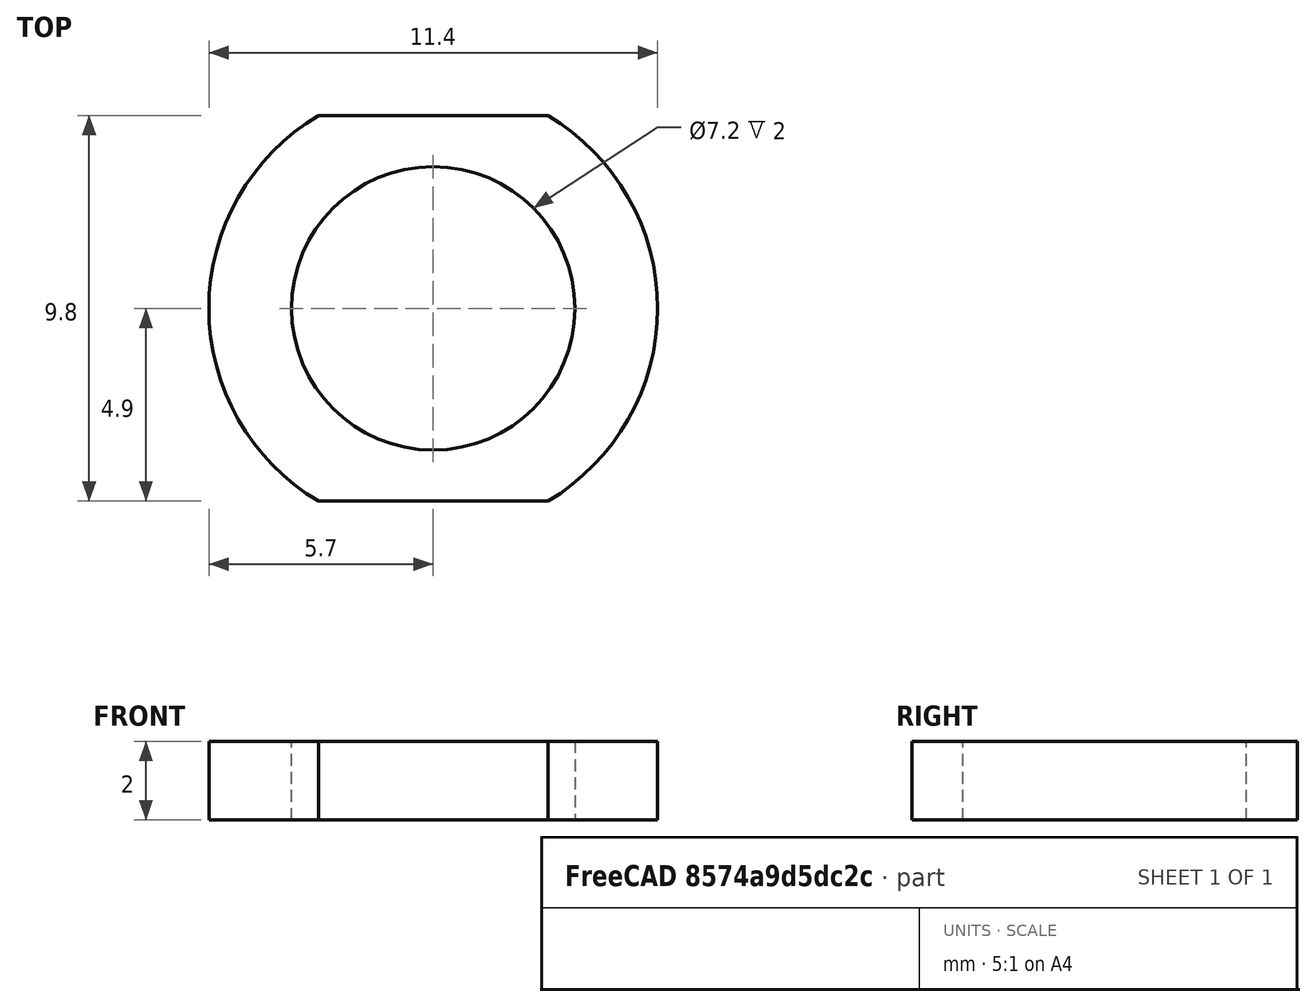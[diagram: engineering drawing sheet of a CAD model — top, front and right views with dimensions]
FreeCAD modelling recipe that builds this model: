
FCSTD DOCUMENT  (FreeCAD 0.18.3R)
Label: lamp.pot.washer
License: All rights reserved
LicenseURL: http://en.wikipedia.org/wiki/All_rights_reserved
objects: Part::Part2DObjectPython×4, Part::Extrusion×4, Part::Cut×2, Part::MultiCommon×1
note: 11 computed .brp shape members not serialized (recipe doc carries the construction recipe); baked Part::Feature solids carry a one-line shape summary decoded from their .brp

FEATURE [Part::Part2DObjectPython] Rectangle  # Draft 2D object (typed FeaturePython)
  ChamferSize = 0
  Columns = 1
  FilletRadius = 0
  Height = 9.8
  Length = 25.8
  MakeFace = true
  Placement = pos=(-12.9,4.9,0) rot=(1,0,0;3.14159rad)
  Rows = 1
FEATURE [Part::Part2DObjectPython] Circle002  # Draft 2D object (typed FeaturePython)
  FirstAngle = 0
  LastAngle = 0
  MakeFace = true
  Placement = pos=(26.0649,8.04739,0) rot=(1,0,0;3.14159rad)
  Radius = 3.5
  Support = -> [Rectangle]
FEATURE [Part::Part2DObjectPython] Circle003  # Draft 2D object (typed FeaturePython)
  FirstAngle = 0
  LastAngle = 0
  MakeFace = true
  Placement = pos=(26.0649,8.04739,0) rot=(1,0,0;3.14159rad)
  Radius = 5.7
FEATURE [Part::Extrusion] Extrude002
  Base = -> Circle002
  Dir = (0,0,-1)
  DirMode = 2
  FaceMakerClass = Part::FaceMakerBullseye
  LengthFwd = -2
  LengthRev = 0
  Solid = false
  Symmetric = false
FEATURE [Part::Extrusion] Extrude003
  Base = -> Circle003
  Dir = (0,0,-1)
  DirMode = 2
  FaceMakerClass = Part::FaceMakerBullseye
  LengthFwd = -2
  LengthRev = 0
  Solid = false
  Symmetric = false
FEATURE [Part::Cut] Cut001
  Base = -> Extrude003
  Placement = pos=(-26.0649,-8.04739,0) rot=(0,0,1;0rad)
  Tool = -> Extrude002
FEATURE [Part::Extrusion] Extrude
  Base = -> Rectangle
  Dir = (0,0,-1)
  DirMode = 2
  FaceMakerClass = Part::FaceMakerBullseye
  LengthFwd = -2
  LengthRev = 0
  Solid = false
  Symmetric = false
FEATURE [Part::MultiCommon] Common
  Shapes = -> [Extrude,Cut001]
FEATURE [Part::Part2DObjectPython] Circle  # Draft 2D object (typed FeaturePython)
  FirstAngle = 0
  LastAngle = 0
  MakeFace = true
  Placement = pos=(1.42e-14,2e-15,2) rot=(0,0,1;0rad)
  Radius = 3.6
FEATURE [Part::Extrusion] Extrude004
  Base = -> Circle
  Dir = (0,0,1)
  DirMode = 2
  FaceMakerClass = Part::FaceMakerBullseye
  LengthFwd = -2
  LengthRev = 0
  Solid = false
  Symmetric = false
FEATURE [Part::Cut] Cut
  Base = -> Common
  Tool = -> Extrude004
